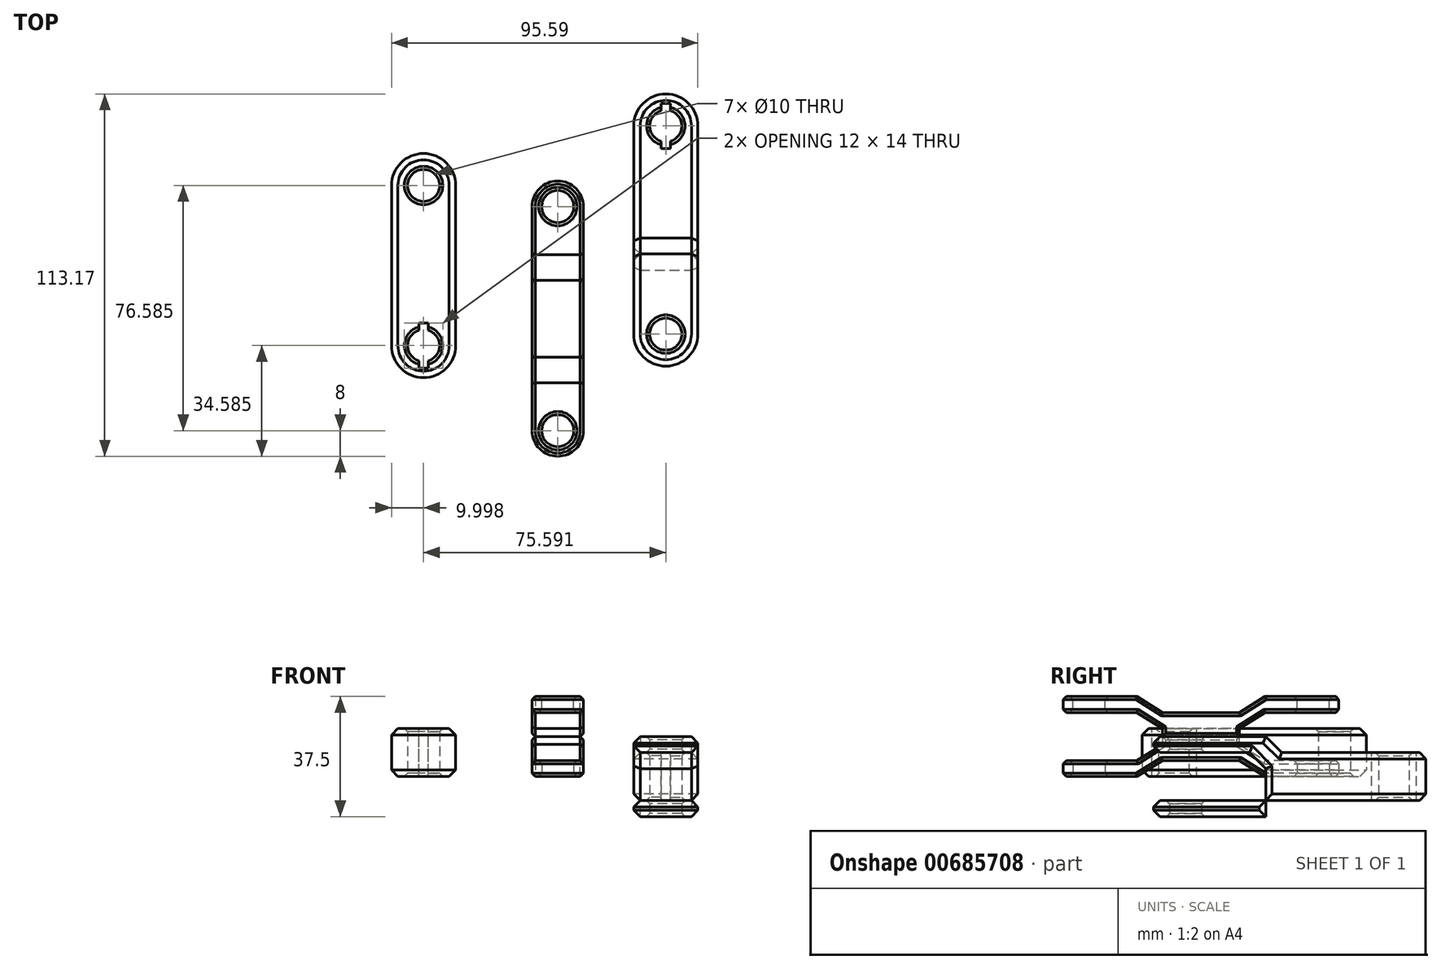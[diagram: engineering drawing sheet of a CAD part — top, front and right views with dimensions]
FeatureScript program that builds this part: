
annotation { "Feature Type Name" : "Feature", "Feature Type Description" : "" }
export const myFeature = defineFeature(function(context is Context, id is Id, definition is map)
    precondition{}
    {
        {
            var Q0;
            Q0=qCreatedBy(makeId("Top.planeOp"),FACE);
            var sketch = newSketch(context, id + "F0", { "sketchPlane" : qUnion([Q0])});
            skCircle(sketch, "E0", {"center": v(0, 0) * mm, "radius": 5 * mm});
            skArc(sketch, "E1", {"start": v(8, 0) * mm, "mid": v(0, 8) * mm, "end": v(-8, 0) * mm});
            skLineSegment(sketch, "E2.top", {"start": v(-8, -15) * mm, "end": v(8, -15) * mm});
            skLineSegment(sketch, "E2.left", {"start": v(-8, 0) * mm, "end": v(-8, -15) * mm});
            skLineSegment(sketch, "E2.right", {"start": v(8, 0) * mm, "end": v(8, -15) * mm});
            skSolve(sketch);
        }
        {
            var Q0;
            Q0=makeQuery(id+"F0.imprint","IMPRINT",FACE,{"disambiguationData":[TD([[makeQuery(id+"F0.imprint","IMPRINT",EDGE,{"derivedFrom":sQuery(id+"F0.wireOp",EDGE,"E0")}),-1.0]])]});
            extrude(context, id + "F1", {"entities" : qUnion([Q0]), "depth" : 5 * mm, "offsetDistance" : 25 * mm});
        }
        {
            var Q0;
            Q0=makeQuery(id+"F1.opExtrude","CAP_FACE",FACE,{"disambiguationData":[OSD([sQuery(id+"F0.wireOp",EDGE,"E0"),sQuery(id+"F0.wireOp",EDGE,"E1"),sQuery(id+"F0.wireOp",EDGE,"E2.top"),sQuery(id+"F0.wireOp",EDGE,"E2.left"),sQuery(id+"F0.wireOp",EDGE,"E2.right")])],"isStart":false});
            cPlane(context, id + "F2", {"entities" : qUnion([Q0]), "cplaneType" : CPlaneType.OFFSET, "offset" : 0 * mm, "width" : 150 * mm, "height" : 150 * mm});
        }
        {
            var Q0;
            Q0=qCreatedBy(id+"F2.planeOp",FACE);
            var sketch = newSketch(context, id + "F3", { "sketchPlane" : qUnion([Q0])});
            skLineSegment(sketch, "E3.bottom", {"start": v(-8, -23) * mm, "end": v(8, -23) * mm});
            skLineSegment(sketch, "E3.top", {"start": v(-8, -35) * mm, "end": v(8, -35) * mm});
            skLineSegment(sketch, "E3.left", {"start": v(-8, -23) * mm, "end": v(-8, -35) * mm});
            skLineSegment(sketch, "E3.right", {"start": v(8, -23) * mm, "end": v(8, -35) * mm});
            skSolve(sketch);
        }
        {
            var Q0;
            Q0=makeQuery(id+"F3.imprint","IMPRINT",FACE,{"disambiguationData":[TD([[makeQuery(id+"F3.imprint","IMPRINT",EDGE,{"derivedFrom":sQuery(id+"F3.wireOp",EDGE,"E3.bottom")}),-1.0]])]});
            extrude(context, id + "F4", {"entities" : qUnion([Q0]), "depth" : 5 * mm, "offsetDistance" : 25 * mm});
        }
        {
            var Q0;
            Q0=makeQuery(id+"F1.opExtrude","SWEPT_FACE",FACE,{"disambiguationData":[OSD([sQuery(id+"F0.wireOp",EDGE,"E2.top")])]});
            var Q1;
            Q1=makeQuery(id+"F4.opExtrude","SWEPT_FACE",FACE,{"disambiguationData":[OSD([sQuery(id+"F3.wireOp",EDGE,"E3.bottom")])]});
            loft(context, id + "F5", {"operationType" : NewBodyOperationType.ADD, "sheetProfilesArray" : [{ "sheetProfileEntities" : qUnion([Q0]) }, { "sheetProfileEntities" : qUnion([Q1]) }]});
        }
        {
            var Q0;
            Q0=makeQuery(id+"F1.opExtrude","SWEPT_BODY",BODY,{"disambiguationData":[OSD([sQuery(id+"F0.wireOp",EDGE,"E0"),sQuery(id+"F0.wireOp",EDGE,"E1"),sQuery(id+"F0.wireOp",EDGE,"E2.top"),sQuery(id+"F0.wireOp",EDGE,"E2.left"),sQuery(id+"F0.wireOp",EDGE,"E2.right")])]});
            var Q1;
            Q1=makeQuery(id+"F4.opExtrude","SWEPT_FACE",FACE,{"disambiguationData":[OSD([sQuery(id+"F3.wireOp",EDGE,"E3.top")])]});
            mirror(context, id + "F6", {"operationType" : NewBodyOperationType.ADD, "entities" : qUnion([Q0]), "mirrorPlane" : qUnion([Q1])});
        }
        {
            var Q0;
            Q0=qCreatedBy(makeId("Top.planeOp"),FACE);
            var sketch = newSketch(context, id + "F7", { "sketchPlane" : qUnion([Q0])});
            skLineSegment(sketch, "E4.left", {"start": v(-51.86, 6.58) * mm, "end": v(-51.86, -43.42) * mm});
            skLineSegment(sketch, "E4.right", {"start": v(-31.86, 6.58) * mm, "end": v(-31.86, -43.42) * mm});
            skArc(sketch, "E5", {"start": v(-51.86, 6.58) * mm, "mid": v(-41.86, 16.58) * mm, "end": v(-31.86, 6.58) * mm});
            skArc(sketch, "E6", {"start": v(-31.86, -43.42) * mm, "mid": v(-41.86, -53.42) * mm, "end": v(-51.86, -43.42) * mm});
            skCircle(sketch, "E7", {"center": v(-41.86, 6.58) * mm, "radius": 5 * mm});
            skCircle(sketch, "E8", {"center": v(-41.86, -43.42) * mm, "radius": 5 * mm});
            skSolve(sketch);
        }
        {
            var Q0;
            Q0=makeQuery(id+"F7.imprint","IMPRINT",FACE,{"disambiguationData":[TD([[makeQuery(id+"F7.imprint","IMPRINT",EDGE,{"derivedFrom":sQuery(id+"F7.wireOp",EDGE,"E4.left")}),1.0]])]});
            extrude(context, id + "F8", {"entities" : qUnion([Q0]), "depth" : 15 * mm, "offsetDistance" : 25 * mm});
        }
        {
            var Q0;
            Q0=makeQuery(id+"F8.opExtrude","CAP_EDGE",EDGE,{"disambiguationData":[OSD([sQuery(id+"F7.wireOp",EDGE,"E4.right")])],"isStart":false});
            var Q1;
            Q1=makeQuery(id+"F8.opExtrude","CAP_EDGE",EDGE,{"disambiguationData":[OSD([sQuery(id+"F7.wireOp",EDGE,"E4.right")])],"isStart":true});
            chamfer(context, id + "F9", {"entities" : qUnion([Q0, Q1]), "width" : 2 * mm, "tangentPropagation" : true});
        }
        {
            var Q0;
            Q0=makeQuery(id+"F8.opExtrude","SWEPT_FACE",FACE,{"disambiguationData":[OSD([sQuery(id+"F7.wireOp",EDGE,"E7")])]});
            var Q1;
            Q1=makeQuery(id+"F8.opExtrude","CAP_EDGE",EDGE,{"disambiguationData":[OSD([sQuery(id+"F7.wireOp",EDGE,"E8")])],"isStart":true});
            var Q2;
            Q2=makeQuery(id+"F8.opExtrude","CAP_EDGE",EDGE,{"disambiguationData":[OSD([sQuery(id+"F7.wireOp",EDGE,"E8")])],"isStart":false});
            chamfer(context, id + "F10", {"entities" : qUnion([Q0, Q1, Q2]), "width" : 1 * mm, "tangentPropagation" : true});
        }
        {
            var Q0;
            Q0=qCreatedBy(makeId("Top.planeOp"),FACE);
            var sketch = newSketch(context, id + "F11", { "sketchPlane" : qUnion([Q0])});
            skLineSegment(sketch, "E9.left", {"start": v(23.73, 25.17) * mm, "end": v(23.73, -39.83) * mm});
            skLineSegment(sketch, "E9.right", {"start": v(43.73, 25.17) * mm, "end": v(43.73, -39.83) * mm});
            skArc(sketch, "E10", {"start": v(43.73, 25.17) * mm, "mid": v(33.73, 35.17) * mm, "end": v(23.73, 25.17) * mm});
            skArc(sketch, "E11", {"start": v(23.73, -39.83) * mm, "mid": v(33.73, -49.83) * mm, "end": v(43.73, -39.83) * mm});
            skCircle(sketch, "E12", {"center": v(33.73, 25.17) * mm, "radius": 5 * mm});
            skCircle(sketch, "E13", {"center": v(33.73, -39.83) * mm, "radius": 5 * mm});
            skPoint(sketch, "E14", {"position": v(43.73, -14.83) * mm});
            skPoint(sketch, "E15", {"position": v(23.73, -14.83) * mm});
            skLineSegment(sketch, "E16", {"start": v(23.73, -14.83) * mm, "end": v(43.73, -14.83) * mm});
            skSolve(sketch);
        }
        {
            var Q0;
            {var subQ0=sQuery(id+"F11.wireOp",EDGE,"E10");Q0=makeQuery(id+"F11.imprint","IMPRINT",FACE,{"disambiguationData":[TD([[makeQuery(id+"F11.imprint","IMPRINT",EDGE,{"derivedFrom":subQ0}),1.0]])]});}
            extrude(context, id + "F12", {"entities" : qUnion([Q0]), "endBound" : BoundingType.SYMMETRIC, "depth" : 15 * mm, "offsetDistance" : 25 * mm});
        }
        {
            var Q0;
            {var subQ0=sQuery(id+"F11.wireOp",EDGE,"E11");Q0=makeQuery(id+"F11.imprint","IMPRINT",FACE,{"disambiguationData":[TD([[makeQuery(id+"F11.imprint","IMPRINT",EDGE,{"derivedFrom":subQ0}),1.0]])]});}
            extrude(context, id + "F13", {"entities" : qUnion([Q0]), "operationType" : NewBodyOperationType.ADD, "endBound" : BoundingType.SYMMETRIC, "depth" : 25 * mm, "offsetDistance" : 25 * mm});
        }
        {
            var Q0;
            Q0=makeQuery(id+"F12.opExtrude","CAP_EDGE",EDGE,{"disambiguationData":[OSD([sQuery(id+"F11.wireOp",EDGE,"E16")])],"isStart":false});
            var Q1;
            Q1=makeQuery(id+"F12.opExtrude","CAP_EDGE",EDGE,{"disambiguationData":[OSD([sQuery(id+"F11.wireOp",EDGE,"E16")])],"isStart":true});
            chamfer(context, id + "F14", {"entities" : qUnion([Q0, Q1]), "width" : 5 * mm, "tangentPropagation" : true});
        }
        {
            var Q0;
            {var subQ0=sQuery(id+"F11.wireOp",EDGE,"E11");Q0=makeQuery(id+"F11.imprint","IMPRINT",FACE,{"disambiguationData":[TD([[makeQuery(id+"F11.imprint","IMPRINT",EDGE,{"derivedFrom":subQ0}),1.0]])]});}
            extrude(context, id + "F15", {"entities" : qUnion([Q0]), "operationType" : NewBodyOperationType.REMOVE, "endBound" : BoundingType.SYMMETRIC, "oppositeDirection" : true, "depth" : 15 * mm, "offsetDistance" : 25 * mm});
        }
        {
            var Q0;
            Q0=makeQuery(id+"F15.boolean.opBoolean","COPY",EDGE,{"derivedFrom":makeQuery(id+"F15.opExtrude","CAP_EDGE",EDGE,{"disambiguationData":[OSD([sQuery(id+"F11.wireOp",EDGE,"E16")])],"isStart":true})});
            var Q1;
            Q1=makeQuery(id+"F15.boolean.opBoolean","COPY",EDGE,{"derivedFrom":makeQuery(id+"F15.opExtrude","CAP_EDGE",EDGE,{"disambiguationData":[OSD([sQuery(id+"F11.wireOp",EDGE,"E16")])],"isStart":false})});
            chamfer(context, id + "F16", {"entities" : qUnion([Q0, Q1]), "width" : 5 * mm, "tangentPropagation" : true});
        }
        {
            var Q0;
            Q0=makeQuery(id+"F12.opExtrude","SWEPT_FACE",FACE,{"disambiguationData":[OSD([sQuery(id+"F11.wireOp",EDGE,"E12")])]});
            var Q1;
            {var subQ0=sQuery(id+"F11.wireOp",EDGE,"E16");var subQ1=sQuery(id+"F11.wireOp",EDGE,"E13");var subQ2=sQuery(id+"F11.wireOp",EDGE,"E11");var subQ3=sQuery(id+"F11.wireOp",EDGE,"E9.right");var subQ4=sQuery(id+"F11.wireOp",EDGE,"E9.left");Q1=makeQuery(id+"F15.boolean.opBoolean","SPLIT",FACE,{"disambiguationData":[TD([makeQuery(id+"F13.opExtrude","CAP_FACE",FACE,{"disambiguationData":[OSD([subQ4,subQ3,subQ2,subQ1,subQ0])],"isStart":false})])],"derivedFrom":makeQuery(id+"F13.opExtrude","SWEPT_FACE",FACE,{"disambiguationData":[OSD([subQ1])]})});}
            var Q2;
            {var subQ0=sQuery(id+"F11.wireOp",EDGE,"E16");var subQ1=sQuery(id+"F11.wireOp",EDGE,"E13");var subQ2=sQuery(id+"F11.wireOp",EDGE,"E11");var subQ3=sQuery(id+"F11.wireOp",EDGE,"E9.right");var subQ4=sQuery(id+"F11.wireOp",EDGE,"E9.left");Q2=makeQuery(id+"F15.boolean.opBoolean","SPLIT",FACE,{"disambiguationData":[TD([makeQuery(id+"F13.opExtrude","CAP_FACE",FACE,{"disambiguationData":[OSD([subQ4,subQ3,subQ2,subQ1,subQ0])],"isStart":true})])],"derivedFrom":makeQuery(id+"F13.opExtrude","SWEPT_FACE",FACE,{"disambiguationData":[OSD([subQ1])]})});}
            chamfer(context, id + "F17", {"entities" : qUnion([Q0, Q1, Q2]), "width" : 1 * mm, "tangentPropagation" : true});
        }
        {
            var Q0;
            {var subQ0=sQuery(id+"F11.wireOp",EDGE,"E9.right");Q0=makeQuery(id+"F13.boolean.opBoolean","MERGE",FACE,{"derivedFrom":[makeQuery(id+"F12.opExtrude","SWEPT_FACE",FACE,{"disambiguationData":[OSD([subQ0])]}),makeQuery(id+"F13.opExtrude","SWEPT_FACE",FACE,{"disambiguationData":[OSD([subQ0])]})]});}
            var Q1;
            {var subQ0=sQuery(id+"F11.wireOp",EDGE,"E9.left");Q1=makeQuery(id+"F13.boolean.opBoolean","MERGE",FACE,{"derivedFrom":[makeQuery(id+"F12.opExtrude","SWEPT_FACE",FACE,{"disambiguationData":[OSD([subQ0])]}),makeQuery(id+"F13.opExtrude","SWEPT_FACE",FACE,{"disambiguationData":[OSD([subQ0])]})]});}
            chamfer(context, id + "F18", {"entities" : qUnion([Q0, Q1]), "width" : 2 * mm, "tangentPropagation" : true});
        }
        {
            var Q0;
            {var subQ0=makeQuery(id+"F4.opExtrude","CAP_FACE",FACE,{"disambiguationData":[OSD([sQuery(id+"F3.wireOp",EDGE,"E3.bottom"),sQuery(id+"F3.wireOp",EDGE,"E3.top"),sQuery(id+"F3.wireOp",EDGE,"E3.left"),sQuery(id+"F3.wireOp",EDGE,"E3.right")])],"isStart":false});Q0=makeQuery(id+"F6.boolean.opBoolean","MERGE",FACE,{"derivedFrom":[subQ0,makeQuery(id+"F6.opPattern","COPY",FACE,{"derivedFrom":subQ0,"instanceName":"1"})]});}
            extrude(context, id + "F19", {"entities" : qUnion([Q0]), "operationType" : NewBodyOperationType.ADD, "depth" : 2.5 * mm, "offsetDistance" : 25 * mm});
        }
        {
            var Q0;
            Q0=makeQuery(id+"F1.opExtrude","SWEPT_BODY",BODY,{"disambiguationData":[OSD([sQuery(id+"F0.wireOp",EDGE,"E0"),sQuery(id+"F0.wireOp",EDGE,"E1"),sQuery(id+"F0.wireOp",EDGE,"E2.top"),sQuery(id+"F0.wireOp",EDGE,"E2.left"),sQuery(id+"F0.wireOp",EDGE,"E2.right")])]});
            var Q1;
            Q1=makeQuery(id+"F19.opExtrude","CAP_FACE",FACE,{"disambiguationData":[OSD([sQuery(id+"F3.wireOp",EDGE,"E3.bottom"),sQuery(id+"F3.wireOp",EDGE,"E3.top"),sQuery(id+"F3.wireOp",EDGE,"E3.left"),sQuery(id+"F3.wireOp",EDGE,"E3.right")])],"isStart":false});
            mirror(context, id + "F20", {"operationType" : NewBodyOperationType.ADD, "entities" : qUnion([Q0]), "mirrorPlane" : qUnion([Q1])});
        }
        {
            var Q0;
            Q0=makeQuery(id+"F20.opPattern","COPY",FACE,{"derivedFrom":makeQuery(id+"F1.opExtrude","SWEPT_FACE",FACE,{"disambiguationData":[OSD([sQuery(id+"F0.wireOp",EDGE,"E0")])]}),"instanceName":"1"});
            var Q1;
            Q1=makeQuery(id+"F1.opExtrude","SWEPT_FACE",FACE,{"disambiguationData":[OSD([sQuery(id+"F0.wireOp",EDGE,"E0")])]});
            var Q2;
            Q2=makeQuery(id+"F20.opPattern","COPY",FACE,{"derivedFrom":makeQuery(id+"F6.opPattern","COPY",FACE,{"derivedFrom":makeQuery(id+"F1.opExtrude","SWEPT_FACE",FACE,{"disambiguationData":[OSD([sQuery(id+"F0.wireOp",EDGE,"E0")])]}),"instanceName":"1"}),"instanceName":"1"});
            var Q3;
            Q3=makeQuery(id+"F6.opPattern","COPY",FACE,{"derivedFrom":makeQuery(id+"F1.opExtrude","SWEPT_FACE",FACE,{"disambiguationData":[OSD([sQuery(id+"F0.wireOp",EDGE,"E0")])]}),"instanceName":"1"});
            chamfer(context, id + "F21", {"entities" : qUnion([Q0, Q1, Q2, Q3]), "width" : 1 * mm, "tangentPropagation" : true});
        }
        {
            var Q0;
            {var subQ0=sQuery(id+"F3.wireOp",EDGE,"E3.left");var subQ1=sQuery(id+"F0.wireOp",EDGE,"E2.left");var subQ2=makeQuery(id+"F5.boolean.opBoolean","MERGE",FACE,{"derivedFrom":[makeQuery(id+"F1.opExtrude","SWEPT_FACE",FACE,{"disambiguationData":[OSD([subQ1])]}),makeQuery(id+"F4.opExtrude","SWEPT_FACE",FACE,{"disambiguationData":[OSD([subQ0])]}),makeQuery(id+"F5.opLoft","SWEPT_FACE",FACE,{"disambiguationData":[OSD([sQuery(id+"F0.wireOp",EDGE,"E2.top"),subQ1,sQuery(id+"F3.wireOp",EDGE,"E3.bottom"),subQ0])]})]});var subQ3=makeQuery(id+"F19.boolean.opBoolean","MERGE",FACE,{"derivedFrom":[makeQuery(id+"F6.boolean.opBoolean","MERGE",FACE,{"derivedFrom":[subQ2,makeQuery(id+"F6.opPattern","COPY",FACE,{"derivedFrom":subQ2,"instanceName":"1"})]}),makeQuery(id+"F19.opExtrude","SWEPT_FACE",FACE,{"disambiguationData":[OSD([subQ0])]})]});Q0=makeQuery(id+"F20.boolean.opBoolean","MERGE",FACE,{"derivedFrom":[subQ3,makeQuery(id+"F20.opPattern","COPY",FACE,{"derivedFrom":subQ3,"instanceName":"1"})]});}
            var Q1;
            {var subQ0=sQuery(id+"F3.wireOp",EDGE,"E3.right");var subQ1=sQuery(id+"F0.wireOp",EDGE,"E2.right");var subQ2=makeQuery(id+"F5.boolean.opBoolean","MERGE",FACE,{"derivedFrom":[makeQuery(id+"F1.opExtrude","SWEPT_FACE",FACE,{"disambiguationData":[OSD([subQ1])]}),makeQuery(id+"F4.opExtrude","SWEPT_FACE",FACE,{"disambiguationData":[OSD([subQ0])]}),makeQuery(id+"F5.opLoft","SWEPT_FACE",FACE,{"disambiguationData":[OSD([sQuery(id+"F0.wireOp",EDGE,"E2.top"),subQ1,sQuery(id+"F3.wireOp",EDGE,"E3.bottom"),subQ0])]})]});var subQ3=makeQuery(id+"F19.boolean.opBoolean","MERGE",FACE,{"derivedFrom":[makeQuery(id+"F6.boolean.opBoolean","MERGE",FACE,{"derivedFrom":[subQ2,makeQuery(id+"F6.opPattern","COPY",FACE,{"derivedFrom":subQ2,"instanceName":"1"})]}),makeQuery(id+"F19.opExtrude","SWEPT_FACE",FACE,{"disambiguationData":[OSD([subQ0])]})]});Q1=makeQuery(id+"F20.boolean.opBoolean","MERGE",FACE,{"derivedFrom":[subQ3,makeQuery(id+"F20.opPattern","COPY",FACE,{"derivedFrom":subQ3,"instanceName":"1"})]});}
            chamfer(context, id + "F22", {"entities" : qUnion([Q0, Q1]), "width" : 1 * mm, "tangentPropagation" : true});
        }
        {
            var Q0;
            Q0=makeQuery(id+"F8.opExtrude","CAP_FACE",FACE,{"disambiguationData":[OSD([sQuery(id+"F7.wireOp",EDGE,"E4.left"),sQuery(id+"F7.wireOp",EDGE,"E4.right"),sQuery(id+"F7.wireOp",EDGE,"E5"),sQuery(id+"F7.wireOp",EDGE,"E6"),sQuery(id+"F7.wireOp",EDGE,"E7"),sQuery(id+"F7.wireOp",EDGE,"E8")])],"isStart":false});
            var sketch = newSketch(context, id + "F23", { "sketchPlane" : qUnion([Q0])});
            skCircle(sketch, "E17.0", {"center": v(-41.86, -43.42) * mm, "radius": 5 * mm});
            skLineSegment(sketch, "E18.bottom", {"start": v(-40.36, -36.42) * mm, "end": v(-43.36, -36.42) * mm});
            skLineSegment(sketch, "E18.top", {"start": v(-40.36, -50.42) * mm, "end": v(-43.36, -50.42) * mm});
            skLineSegment(sketch, "E18.left", {"start": v(-40.36, -36.42) * mm, "end": v(-40.36, -50.42) * mm});
            skLineSegment(sketch, "E18.right", {"start": v(-43.36, -36.42) * mm, "end": v(-43.36, -50.42) * mm});
            skSolve(sketch);
        }
        {
            var Q0;
            {var subQ0=sQuery(id+"F23.wireOp",EDGE,"E18.bottom");Q0=makeQuery(id+"F23.imprint","IMPRINT",FACE,{"disambiguationData":[TD([[makeQuery(id+"F23.imprint","IMPRINT",EDGE,{"derivedFrom":subQ0}),1.0]])]});}
            var Q1;
            {var subQ0=sQuery(id+"F23.wireOp",EDGE,"E18.right");var subQ1=sQuery(id+"F23.wireOp",EDGE,"E17.0");var subQ2=makeQuery(id+"F23.imprint","INTERSECT",VERTEX,{"disambiguationData":[OD(0.0)],"derivedFrom":[subQ1,subQ0]});Q1=makeQuery(id+"F23.imprint","IMPRINT",FACE,{"disambiguationData":[TD([[makeQuery(id+"F23.imprint","IMPRINT",EDGE,{"disambiguationData":[TD([[subQ2,1.0]])],"derivedFrom":subQ1}),-1.0]])]});}
            var Q2;
            {var subQ0=sQuery(id+"F23.wireOp",EDGE,"E18.right");var subQ1=sQuery(id+"F23.wireOp",EDGE,"E17.0");var subQ2=makeQuery(id+"F23.imprint","INTERSECT",VERTEX,{"disambiguationData":[OD(1.0)],"derivedFrom":[subQ1,subQ0]});Q2=makeQuery(id+"F23.imprint","IMPRINT",FACE,{"disambiguationData":[TD([[makeQuery(id+"F23.imprint","IMPRINT",EDGE,{"disambiguationData":[TD([[subQ2,-1.0]])],"derivedFrom":subQ1}),-1.0]])]});}
            var Q3;
            {var subQ0=sQuery(id+"F23.wireOp",EDGE,"E18.top");Q3=makeQuery(id+"F23.imprint","IMPRINT",FACE,{"disambiguationData":[TD([[makeQuery(id+"F23.imprint","IMPRINT",EDGE,{"derivedFrom":subQ0}),-1.0]])]});}
            extrude(context, id + "F24", {"entities" : qUnion([Q0, Q1, Q2, Q3]), "operationType" : NewBodyOperationType.REMOVE, "oppositeDirection" : true, "depth" : 15 * mm, "offsetDistance" : 25 * mm});
        }
        {
            var Q0;
            Q0=makeQuery(id+"F12.opExtrude","CAP_FACE",FACE,{"disambiguationData":[OSD([sQuery(id+"F11.wireOp",EDGE,"E9.left"),sQuery(id+"F11.wireOp",EDGE,"E9.right"),sQuery(id+"F11.wireOp",EDGE,"E10"),sQuery(id+"F11.wireOp",EDGE,"E12"),sQuery(id+"F11.wireOp",EDGE,"E16")])],"isStart":false});
            var sketch = newSketch(context, id + "F25", { "sketchPlane" : qUnion([Q0])});
            skCircle(sketch, "E19.0", {"center": v(33.73, 25.17) * mm, "radius": 6 * mm});
            skLineSegment(sketch, "E20.bottom", {"start": v(35.23, 32.17) * mm, "end": v(32.23, 32.17) * mm});
            skLineSegment(sketch, "E20.top", {"start": v(35.23, 18.17) * mm, "end": v(32.23, 18.17) * mm});
            skLineSegment(sketch, "E20.left", {"start": v(35.23, 32.17) * mm, "end": v(35.23, 18.17) * mm});
            skLineSegment(sketch, "E20.right", {"start": v(32.23, 32.17) * mm, "end": v(32.23, 18.17) * mm});
            skSolve(sketch);
        }
        {
            var Q0;
            {var subQ5=sQuery(id+"F25.wireOp",EDGE,"E20.top");Q0=makeQuery(id+"F25.imprint","IMPRINT",FACE,{"disambiguationData":[TD([[makeQuery(id+"F25.imprint","IMPRINT",EDGE,{"derivedFrom":subQ5}),-1.0]])]});}
            var Q1;
            {var subQ0=sQuery(id+"F25.wireOp",EDGE,"E20.right");var subQ1=sQuery(id+"F25.wireOp",EDGE,"E19.0");var subQ2=makeQuery(id+"F25.imprint","INTERSECT",VERTEX,{"disambiguationData":[OD(0.0)],"derivedFrom":[subQ1,subQ0]});Q1=makeQuery(id+"F25.imprint","IMPRINT",FACE,{"disambiguationData":[TD([[makeQuery(id+"F25.imprint","IMPRINT",EDGE,{"disambiguationData":[TD([[subQ2,-1.0]])],"derivedFrom":subQ1}),-1.0]])]});}
            var Q2;
            {var subQ5=sQuery(id+"F25.wireOp",EDGE,"E20.bottom");Q2=makeQuery(id+"F25.imprint","IMPRINT",FACE,{"disambiguationData":[TD([[makeQuery(id+"F25.imprint","IMPRINT",EDGE,{"derivedFrom":subQ5}),1.0]])]});}
            extrude(context, id + "F26", {"entities" : qUnion([Q0, Q1, Q2]), "operationType" : NewBodyOperationType.REMOVE, "oppositeDirection" : true, "depth" : 15 * mm, "offsetDistance" : 25 * mm});
        }
    });
